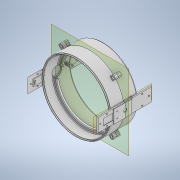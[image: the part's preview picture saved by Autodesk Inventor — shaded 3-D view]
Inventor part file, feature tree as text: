
AUTODESK INVENTOR PART (.ipt)
format: ipt  version: 2020.2 (Build 242310000, 310)  size: 974,336 bytes
history: native  units: mm
features: extrude x26, sketch x26, reference x21, other x8, plane x6, chamfer x3, pattern_circular x2, mirror x1, split x1
ambient origin geometry x8: Origin, YZ Plane, XZ Plane, XY Plane, X Axis, Y Axis, Z Axis, Center Point
bodies: Solid1 (feature_tree), Solid2 (feature_tree), Solid3 (feature_tree)
feature tree (94):
  extrude  "Extrusion1"  Depth=205.0mm
  extrude  "Extrusion2"  Depth=40.0mm
  plane  "Work Plane4"
  extrude  "Extrusion3"  Depth=3.0mm TaperAngle=0.0deg
  extrude  "Extrusion4"  Depth=45.0mm
  extrude  "Extrusion6"  TaperAngle=0.0deg  [1 undecoded]
  extrude  "Extrusion8"  Depth=2.0mm
  chamfer  "Chamfer1"  Distance=20.0mm Angle=360.0deg
  pattern_circular  "Circular Pattern1"  Count=8  [1 undecoded]
  mirror  "Mirror1"
  plane  "Work Plane6"
  plane  "Work Plane8"
  extrude  "Extrusion15"  Depth=40.0mm
  extrude  "Extrusion16"  Depth=1.0mm
  extrude  "Extrusion17"  Depth=8.0mm
  extrude  "Extrusion20"  Depth=20.0mm TaperAngle=0.0deg
  chamfer  "Chamfer2"  Distance=5.0mm
  pattern_circular  "Circular Pattern2"  Count=2 Angle=360.0deg
  extrude  "Extrusion19"  Depth=191.666667mm
  extrude  "Extrusion21"  Depth=3.0mm TaperAngle=0.0deg
  extrude  "Extrusion22"  Depth=2.0mm
  extrude  "Extrusion23"  Depth=0.4mm
  extrude  "Extrusion24"  Depth=6.0mm
  plane  "Work Plane10"
  extrude  "Extrusion25"  TaperAngle=0.0deg  [1 undecoded]
  extrude  "Extrusion26"  TaperAngle=0.0deg  [1 undecoded]
  extrude  "Extrusion27"  TaperAngle=0.0deg  [1 undecoded]
  extrude  "Extrusion28"  Depth=6.0mm
  extrude  "Extrusion29"  Depth=2.0mm TaperAngle=0.0deg
  extrude  "Extrusion30"  Depth=2.0mm TaperAngle=0.0deg
  extrude  "Extrusion34"  Depth=2.0mm TaperAngle=0.0deg
  extrude  "Extrusion35"  Depth=2.0mm
  plane  "Work Plane11"
  extrude  "Extrusion36"  Depth=2.0mm
  extrude  "Extrusion37"  Depth=6.0mm TaperAngle=0.0deg
  extrude  "Extrusion38"  [1 undecoded]
  chamfer  "Chamfer3"  Distance=16.0mm
  split  "Split1"
  sketch  "Sketch1"  dims[d0=215.0mm d1=205.0mm]
  sketch  "Sketch2"  dims[d2=40.0mm d3=0.0mm d4=208.633333mm]
  plane  "Work Plane3"
  sketch  "Sketch4"  dims[d5=211.366667mm d6=3.0mm d7=0.0mm]
  sketch  "Sketch5"  dims[d8=45.0mm d9=45.0mm]
  reference  "Reference1"
  sketch  "Sketch6"  dims[d10=3.0mm d11=0.0mm d12=0.0mm]
  sketch  "Sketch8"  dims[d13=2.0mm d14=0.0mm d17=0.1mm]
  reference  "Reference7"
  reference  "Reference8"
  reference  "Reference9"
  reference  "Reference10"
  sketch  "Sketch16"  dims[d18=1.9mm]
  sketch  "Sketch17"  dims[d19=0.0mm d23=20.0mm d24=360.0deg]
  reference  "Reference12"
  reference  "Reference13"
  sketch  "Sketch18"  dims[d26=0.1mm]
  sketch  "Sketch20"  dims[d27=1.0mm d28=0.0mm]
  sketch  "Sketch21"  dims[d29=2.0mm d30=2.0mm d31=45.0deg]
  sketch  "Sketch22"  dims[d67=30.2mm]
  sketch  "Sketch23"  dims[d68=41.0mm d69=80.0mm]
  reference  "Reference14"
  reference  "Reference15"
  sketch  "Sketch24"  dims[d70=40.0mm d71=20.5mm]
  sketch  "Sketch25"  dims[d72=215.0mm d73=0.0mm d74=1.0mm]
  reference  "Reference16"
  reference  "Reference17"
  sketch  "Sketch26"  dims[d75=4.0mm d76=8.0mm]
  reference  "Reference18"
  reference  "Reference19"
  sketch  "Sketch27"  dims[d77=26.0mm d78=20.0mm d79=0.0mm]
  reference  "Reference20"
  reference  "Reference21"
  sketch  "Sketch28"  dims[d80=10.0mm d83=5.0mm d84=0.0mm]
  sketch  "Sketch29"  dims[d85=0.0mm]
  reference  "Reference22"
  reference  "Reference23"
  reference  "Reference24"
  reference  "Reference25"
  sketch  "Sketch30"  dims[d86=2.5mm d87=0.0mm d97=20.0mm d98=360.0deg]
  reference  "Reference26"
  reference  "Reference27"
  sketch  "Sketch31"  dims[d100=215.0mm d101=0.0mm d102=191.666667mm]
  sketch  "Sketch35"  dims[d103=198.333333mm d104=3.0mm d105=0.0mm]
  sketch  "Sketch36"  dims[d106=2.0mm d107=2.0mm d108=45.0deg d110=20.0mm]
  sketch  "Sketch39"  dims[d111=72.5mm d112=0.0mm d114=0.4mm]
  sketch  "Sketch40"  dims[d115=6.0mm d116=6.8mm]
  sketch  "Sketch41"  dims[d117=6.8mm d118=0.0mm d119=0.0mm d120=0.0mm d121=6.0mm d122=4.0mm d123=0.0mm d124=7.5mm d125=0.0mm d126=3.0mm d127=0.0mm d128=2.0mm d129=2.0mm d130=6.0mm d131=0.0mm d132=-7.0mm d133=16.0mm d134=8.0mm d135=0.5mm d136=40.0mm d137=30.2mm d138=3.0mm d139=22.0mm d140=0.0mm d141=2.0mm d142=2.0mm d143=10.0mm d144=0.0mm d145=5.0mm d146=5.0mm d147=4.0mm d148=0.0mm d149=100.0mm d150=0.0mm d151=57.0mm d153=10.0mm d154=1.8mm d155=0.0mm d156=10.0mm d157=0.0mm d158=3.0mm d159=3.0mm d160=5.0mm d161=0.0mm d162=1.5mm d163=0.0mm d176=28.0mm d177=20.0mm d178=6.0mm d179=4.0mm d180=30.0mm d181=1.0mm d182=0.0mm d183=1.0mm d184=0.0mm d185=12.0mm d186=14.0mm d187=4.0mm d188=40.0mm d190=360.0deg d192=20.0mm d193=0.0mm d194=7.0mm d195=40.0mm d197=360.0deg d199=4.0mm d200=0.0mm d201=8.0mm d202=40.0mm d204=360.0deg d206=5.0mm d207=0.0mm d208=3.0mm d209=2.0mm d210=45.0deg d88=0.872665mm]
  other  "<userpath>\OneDrive\Apps\0011_VentControlValve\Assembly.iam"
  other  "Assembly.iam"
  other  "Base:1"
  other  "<userpath>\OneDrive\Apps\0011_VentControlValve\Drawings\Assembly.iam"
  other  "Butterfly Valve:1"
  other  "limitSwitch:2"
  other  "limitSwitch:1"
  other  "motor+Gearbox:1"
note: 6 required parameter values undecoded (feature->parameter linkage not recoverable at this tier; creation-order binding heuristic only, values carry confidence <= 0.55)
